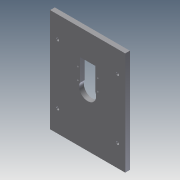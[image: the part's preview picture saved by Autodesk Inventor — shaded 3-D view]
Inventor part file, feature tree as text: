
AUTODESK INVENTOR PART (.ipt)
format: ipt  version: 2011 (Build 150239000, 239)  size: 481,792 bytes
history: native  units: in
note: dims shown in document units (in); Inventor stores cm internally (conversion verified against a paired STEP export)
features: extrude x47, sketch x47, fillet x2
ambient origin geometry x8: Origin, YZ Plane, XZ Plane, XY Plane, X Axis, Y Axis, Z Axis, Center Point
bodies: Solid1 (feature_tree)
feature tree (96):
  extrude  "Extrusion1"  Depth=4.0in
  extrude  "Extrusion2"  Depth=2.16in
  extrude  "Extrusion3"  Depth=1.7655in
  extrude  "Extrusion4"  Depth=0.029in TaperAngle=0.0deg
  extrude  "Extrusion5"  Depth=2.36in
  fillet  "Fillet1"  Radius=2.56in
  extrude  "Extrusion6"  Depth=0.125in
  extrude  "Extrusion7"  Depth=0.262in TaperAngle=0.0deg
  extrude  "Extrusion8"  Depth=0.029in TaperAngle=0.0deg
  extrude  "Extrusion9"  Depth=0.156in
  extrude  "Extrusion10"  Depth=0.5in TaperAngle=0.0deg
  extrude  "Extrusion11"  Depth=0.5in TaperAngle=0.0deg
  extrude  "Extrusion12"  Depth=1.875in TaperAngle=0.0deg
  extrude  "Extrusion13"  Depth=2.125in TaperAngle=0.0deg
  sketch  "Sketch14"  dims[d44=2.125in d45=0.0in d46=2.125in d47=0.0in]
  sketch  "Sketch15"  dims[d48=2.125in d49=0.0in d50=1.875in d51=0.0in]
  sketch  "Sketch16"  dims[d52=2.125in d53=0.0in d54=2.125in d55=0.0in]
  sketch  "Sketch17"  dims[d56=1.875in d57=0.0in d58=1.875in d59=0.0in]
  extrude  "Extrusion14"  Depth=2.125in TaperAngle=0.0deg
  extrude  "Extrusion15"  Depth=1.875in TaperAngle=0.0deg
  extrude  "Extrusion16"  Depth=2.125in TaperAngle=0.0deg
  extrude  "Extrusion17"  Depth=1.875in TaperAngle=0.0deg
  extrude  "Extrusion18"  Depth=2.125in TaperAngle=0.0deg
  extrude  "Extrusion19"  Depth=6.248in TaperAngle=0.0deg
  extrude  "Extrusion20"  Depth=1.281in
  extrude  "Extrusion21"  Depth=7.0in TaperAngle=0.0deg
  extrude  "Extrusion22"  Depth=2.0in
  extrude  "Extrusion23"  Depth=4.0in
  extrude  "Extrusion24"  Depth=2.0in
  extrude  "Extrusion25"  Depth=1.0in TaperAngle=0.0deg
  extrude  "Extrusion26"  Depth=0.25in
  extrude  "Extrusion27"  Depth=0.25in TaperAngle=0.0deg
  extrude  "Extrusion28"  Depth=0.25in TaperAngle=0.0deg
  extrude  "Extrusion29"  Depth=0.875in
  extrude  "Extrusion30"  Depth=0.5in TaperAngle=0.0deg
  extrude  "Extrusion31"  Depth=0.875in
  extrude  "Extrusion32"  Depth=0.5in TaperAngle=0.0deg
  extrude  "Extrusion33"  Depth=2.0in
  extrude  "Extrusion34"  Depth=4.0in
  fillet  "Fillet2"  Radius=1.0in
  extrude  "Extrusion35"  Depth=0.75in TaperAngle=0.0deg
  extrude  "Extrusion36"  Depth=0.9055in
  extrude  "Extrusion37"  Depth=0.8268in
  extrude  "Extrusion38"  Depth=0.75in TaperAngle=0.0deg
  extrude  "Extrusion39"  Depth=0.2559in
  extrude  "Extrusion40"  Depth=0.315in
  extrude  "Extrusion41"  Depth=1.063in
  extrude  "Extrusion42"  Depth=1.0in TaperAngle=0.0deg
  extrude  "Extrusion43"  [1 undecoded]
  extrude  "Extrusion44"  [1 undecoded]
  extrude  "Extrusion45"  [1 undecoded]
  extrude  "Extrusion46"  [1 undecoded]
  extrude  "Extrusion47"  [1 undecoded]
  sketch  "Sketch1"  dims[d0=4.0in d1=4.0in]
  sketch  "Sketch2"  dims[d2=0.029in d3=0.0in d4=2.16in]
  sketch  "Sketch3"  dims[d5=0.029in d6=0.0in d7=1.7655in]
  sketch  "Sketch4"  dims[d8=0.156in d9=0.029in d10=0.0in]
  sketch  "Sketch5"  dims[d11=0.029in d12=0.0in d13=2.36in d14=2.56in]
  sketch  "Sketch6"  dims[d15=0.262in d16=0.0in d17=0.125in]
  sketch  "Sketch7"  dims[d18=0.362in d19=0.0in d20=0.262in d21=0.0in]
  sketch  "Sketch8"  dims[d22=0.1in d23=0.0in d24=0.029in d25=0.0in]
  sketch  "Sketch9"  dims[d26=1.594in d27=0.156in]
  sketch  "Sketch10"  dims[d28=0.029in d29=0.0in d30=0.5in d31=0.0in]
  sketch  "Sketch11"  dims[d32=0.75in d33=0.0in d34=0.5in d35=0.0in]
  sketch  "Sketch12"  dims[d36=2.125in d37=0.0in d38=1.875in d39=0.0in]
  sketch  "Sketch13"  dims[d40=1.875in d41=0.0in d42=2.125in d43=0.0in]
  sketch  "Sketch18"  dims[d60=2.125in d61=0.0in d62=2.125in d63=0.0in]
  sketch  "Sketch19"  dims[d64=0.875in d65=0.0in d66=6.248in d67=0.0in]
  sketch  "Sketch20"  dims[d68=7.0in d69=0.0in d70=1.281in]
  sketch  "Sketch21"  dims[d71=3.188in d72=7.0in d73=0.0in]
  sketch  "Sketch22"  dims[d74=0.25in d75=0.0in d76=2.0in]
  sketch  "Sketch23"  dims[d77=2.0in d78=4.0in]
  sketch  "Sketch24"  dims[d79=1.0in d80=0.0in d81=2.0in]
  sketch  "Sketch25"  dims[d82=1.0in d83=1.0in d84=0.0in]
  sketch  "Sketch26"  dims[d85=0.5in d86=0.25in]
  sketch  "Sketch27"  dims[d87=0.25in d88=0.25in d89=0.0in]
  sketch  "Sketch28"  dims[d90=0.25in d91=0.0in d92=0.25in d93=0.0in]
  sketch  "Sketch29"  dims[d94=0.656in d95=0.875in]
  sketch  "Sketch30"  dims[d96=0.5in d97=0.0in d98=0.5in d99=0.0in]
  sketch  "Sketch31"  dims[d100=0.875in d101=0.875in]
  sketch  "Sketch32"  dims[d102=0.5in d103=0.0in d104=0.5in d105=0.0in]
  sketch  "Sketch33"  dims[d106=2.0in d107=2.0in]
  sketch  "Sketch34"  dims[d108=4.0in d109=4.0in d110=1.0in d111=0.0in]
  sketch  "Sketch35"  dims[d112=0.25in d113=0.0in d114=0.75in d115=0.0in]
  sketch  "Sketch36"  dims[d116=0.75in d117=0.0in d118=0.9055in]
  sketch  "Sketch37"  dims[d119=0.4134in d120=0.8268in]
  sketch  "Sketch38"  dims[d121=1.378in d122=0.75in d123=0.0in]
  sketch  "Sketch39"  dims[d124=0.5315in d125=0.2559in]
  sketch  "Sketch40"  dims[d126=0.315in d127=0.315in]
  sketch  "Sketch41"  dims[d128=1.063in d129=1.063in]
  sketch  "Sketch42"  dims[d130=0.0787in d131=1.0in d132=0.0in]
  sketch  "Sketch43"
  sketch  "Sketch44"
  sketch  "Sketch45"
  sketch  "Sketch46"
  sketch  "Sketch47"
note: 5 required parameter values undecoded (feature->parameter linkage not recoverable at this tier; creation-order binding heuristic only, values carry confidence <= 0.55)
